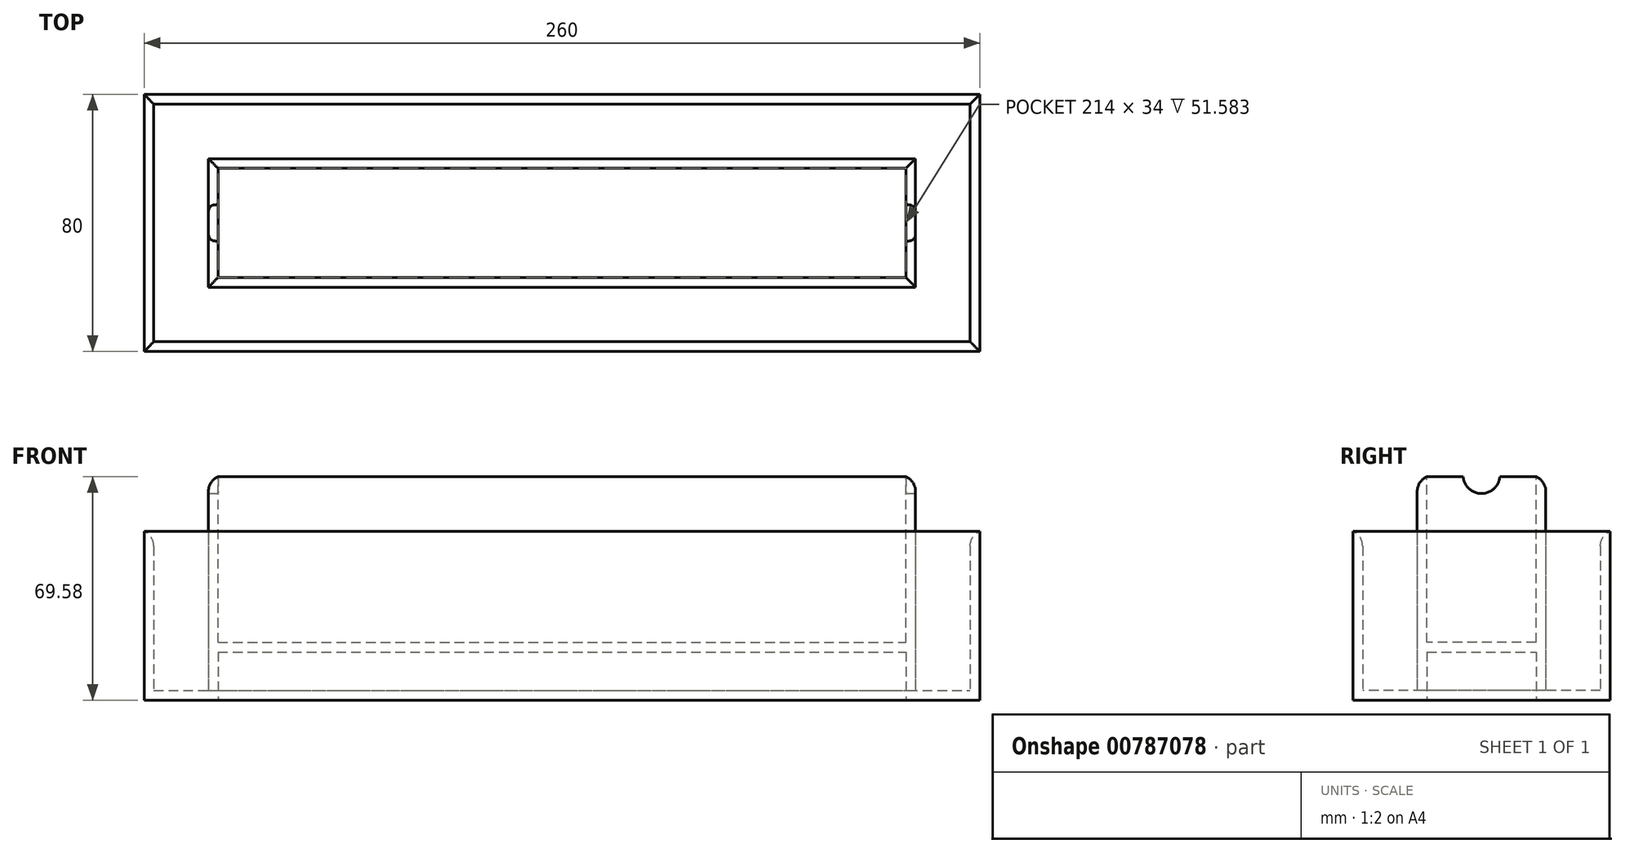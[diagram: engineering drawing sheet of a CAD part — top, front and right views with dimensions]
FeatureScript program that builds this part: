
annotation { "Feature Type Name" : "Feature", "Feature Type Description" : "" }
export const myFeature = defineFeature(function(context is Context, id is Id, definition is map)
    precondition{}
    {
        {
            var Q0;
            Q0=qCreatedBy(makeId("Top.planeOp"),FACE);
            var sketch = newSketch(context, id + "F0", { "sketchPlane" : qUnion([Q0])});
            skLineSegment(sketch, "E0.bottom", {"start": v(-130, 40) * mm, "end": v(130, 40) * mm});
            skLineSegment(sketch, "E0.top", {"start": v(-130, -40) * mm, "end": v(130, -40) * mm});
            skLineSegment(sketch, "E0.left", {"start": v(-130, 40) * mm, "end": v(-130, -40) * mm});
            skLineSegment(sketch, "E0.right", {"start": v(130, 40) * mm, "end": v(130, -40) * mm});
            skSolve(sketch);
        }
        {
            var Q0;
            Q0 = qSketchRegion(id + "F0", true);
            extrude(context, id + "F1", {"entities" : qUnion([Q0]), "depth" : 1 * mm, "offsetDistance" : 25 * mm});
        }
        {
            var Q0;
            Q0=makeQuery(id+"F1.opExtrude","CAP_FACE",FACE,{"disambiguationData":[OSD([sQuery(id+"F0.wireOp",EDGE,"E0.bottom"),sQuery(id+"F0.wireOp",EDGE,"E0.top"),sQuery(id+"F0.wireOp",EDGE,"E0.left"),sQuery(id+"F0.wireOp",EDGE,"E0.right")])],"isStart":false});
            var sketch = newSketch(context, id + "F2", { "sketchPlane" : qUnion([Q0])});
            skLineSegment(sketch, "E1.bottom", {"start": v(-130, 40) * mm, "end": v(-120, 40) * mm});
            skLineSegment(sketch, "E1.top", {"start": v(-130, 30) * mm, "end": v(-120, 30) * mm});
            skLineSegment(sketch, "E1.left", {"start": v(-130, 40) * mm, "end": v(-130, 30) * mm});
            skLineSegment(sketch, "E1.right", {"start": v(-120, 40) * mm, "end": v(-120, 30) * mm});
            skLineSegment(sketch, "E2.bottom", {"start": v(130, 40) * mm, "end": v(120, 40) * mm});
            skLineSegment(sketch, "E2.top", {"start": v(130, 30) * mm, "end": v(120, 30) * mm});
            skLineSegment(sketch, "E2.left", {"start": v(130, 40) * mm, "end": v(130, 30) * mm});
            skLineSegment(sketch, "E2.right", {"start": v(120, 40) * mm, "end": v(120, 30) * mm});
            skLineSegment(sketch, "E3.bottom", {"start": v(-130, -40) * mm, "end": v(-120, -40) * mm});
            skLineSegment(sketch, "E3.top", {"start": v(-130, -30) * mm, "end": v(-120, -30) * mm});
            skLineSegment(sketch, "E3.left", {"start": v(-130, -40) * mm, "end": v(-130, -30) * mm});
            skLineSegment(sketch, "E3.right", {"start": v(-120, -40) * mm, "end": v(-120, -30) * mm});
            skLineSegment(sketch, "E4.bottom", {"start": v(130, -40) * mm, "end": v(120, -40) * mm});
            skLineSegment(sketch, "E4.top", {"start": v(130, -30) * mm, "end": v(120, -30) * mm});
            skLineSegment(sketch, "E4.left", {"start": v(130, -40) * mm, "end": v(130, -30) * mm});
            skLineSegment(sketch, "E4.right", {"start": v(120, -40) * mm, "end": v(120, -30) * mm});
            skSolve(sketch);
        }
        {
            var Q0;
            Q0 = qSketchRegion(id + "F2", true);
            extrude(context, id + "F3", {"entities" : qUnion([Q0]), "operationType" : NewBodyOperationType.ADD, "depth" : 50 * mm, "offsetDistance" : 25 * mm});
        }
        {
            var Q0;
            Q0=makeQuery(id+"F1.opExtrude","CAP_FACE",FACE,{"disambiguationData":[OSD([sQuery(id+"F0.wireOp",EDGE,"E0.bottom"),sQuery(id+"F0.wireOp",EDGE,"E0.top"),sQuery(id+"F0.wireOp",EDGE,"E0.left"),sQuery(id+"F0.wireOp",EDGE,"E0.right")])],"isStart":true});
            shell(context, id + "F4", {"entities" : qUnion([Q0]), "thickness" : 1 * mm});
        }
        {
            var Q0;
            Q0=makeQuery(id+"F3.opExtrude","CAP_FACE",FACE,{"disambiguationData":[OSD([sQuery(id+"F2.wireOp",EDGE,"E3.bottom"),sQuery(id+"F2.wireOp",EDGE,"E3.top"),sQuery(id+"F2.wireOp",EDGE,"E3.left"),sQuery(id+"F2.wireOp",EDGE,"E3.right")])],"isStart":false});
            var sketch = newSketch(context, id + "F5", { "sketchPlane" : qUnion([Q0])});
            skLineSegment(sketch, "E5.bottom", {"start": v(-130, -40) * mm, "end": v(130, -40) * mm});
            skLineSegment(sketch, "E5.top", {"start": v(-130, 40) * mm, "end": v(130, 40) * mm});
            skLineSegment(sketch, "E5.left", {"start": v(-130, -40) * mm, "end": v(-130, 40) * mm});
            skLineSegment(sketch, "E5.right", {"start": v(130, -40) * mm, "end": v(130, 40) * mm});
            skSolve(sketch);
        }
        {
            var Q0;
            Q0 = qSketchRegion(id + "F5", true);
            extrude(context, id + "F6", {"entities" : qUnion([Q0]), "operationType" : NewBodyOperationType.ADD, "depth" : 3 * mm, "offsetDistance" : 25 * mm});
        }
        {
            var Q0;
            Q0=makeQuery(id+"F6.opExtrude","CAP_FACE",FACE,{"disambiguationData":[OSD([sQuery(id+"F5.wireOp",EDGE,"E5.bottom"),sQuery(id+"F5.wireOp",EDGE,"E5.top"),sQuery(id+"F5.wireOp",EDGE,"E5.left"),sQuery(id+"F5.wireOp",EDGE,"E5.right")])],"isStart":false});
            var sketch = newSketch(context, id + "F7", { "sketchPlane" : qUnion([Q0])});
            skLineSegment(sketch, "E6.bottom", {"start": v(-130, 40) * mm, "end": v(130, 40) * mm});
            skLineSegment(sketch, "E6.top", {"start": v(-130, -40) * mm, "end": v(130, -40) * mm});
            skLineSegment(sketch, "E6.left", {"start": v(-130, 40) * mm, "end": v(-130, -40) * mm});
            skLineSegment(sketch, "E6.right", {"start": v(130, 40) * mm, "end": v(130, -40) * mm});
            skLineSegment(sketch, "E7.bottom", {"start": v(-127, 37) * mm, "end": v(127, 37) * mm});
            skLineSegment(sketch, "E7.top", {"start": v(-127, -37) * mm, "end": v(127, -37) * mm});
            skLineSegment(sketch, "E7.left", {"start": v(-127, 37) * mm, "end": v(-127, -37) * mm});
            skLineSegment(sketch, "E7.right", {"start": v(127, 37) * mm, "end": v(127, -37) * mm});
            skSolve(sketch);
        }
        {
            var Q0;
            Q0 = qSketchRegion(id + "F7", true);
            extrude(context, id + "F8", {"entities" : qUnion([Q0]), "operationType" : NewBodyOperationType.ADD, "depth" : 50 * mm, "offsetDistance" : 25 * mm});
        }
        {
            var Q0;
            Q0=makeQuery(id+"F6.opExtrude","CAP_FACE",FACE,{"disambiguationData":[OSD([sQuery(id+"F5.wireOp",EDGE,"E5.bottom"),sQuery(id+"F5.wireOp",EDGE,"E5.top"),sQuery(id+"F5.wireOp",EDGE,"E5.left"),sQuery(id+"F5.wireOp",EDGE,"E5.right")])],"isStart":false});
            var sketch = newSketch(context, id + "F9", { "sketchPlane" : qUnion([Q0])});
            skLineSegment(sketch, "E8.bottom", {"start": v(-110, 20) * mm, "end": v(110, 20) * mm});
            skLineSegment(sketch, "E8.top", {"start": v(-110, -20) * mm, "end": v(110, -20) * mm});
            skLineSegment(sketch, "E8.left", {"start": v(-110, 20) * mm, "end": v(-110, -20) * mm});
            skLineSegment(sketch, "E8.right", {"start": v(110, 20) * mm, "end": v(110, -20) * mm});
            skSolve(sketch);
        }
        {
            var Q0;
            Q0 = qSketchRegion(id + "F9", true);
            extrude(context, id + "F10", {"entities" : qUnion([Q0]), "operationType" : NewBodyOperationType.ADD, "depth" : 67 * mm, "offsetDistance" : 25 * mm});
        }
        {
            var Q0;
            Q0=makeQuery(id+"F10.opExtrude","CAP_FACE",FACE,{"disambiguationData":[OSD([sQuery(id+"F9.wireOp",EDGE,"E8.bottom"),sQuery(id+"F9.wireOp",EDGE,"E8.top"),sQuery(id+"F9.wireOp",EDGE,"E8.left"),sQuery(id+"F9.wireOp",EDGE,"E8.right")])],"isStart":false});
            var sketch = newSketch(context, id + "F11", { "sketchPlane" : qUnion([Q0])});
            skLineSegment(sketch, "E9.bottom", {"start": v(-107, 17) * mm, "end": v(107, 17) * mm});
            skLineSegment(sketch, "E9.top", {"start": v(-107, -17) * mm, "end": v(107, -17) * mm});
            skLineSegment(sketch, "E9.left", {"start": v(-107, 17) * mm, "end": v(-107, -17) * mm});
            skLineSegment(sketch, "E9.right", {"start": v(107, 17) * mm, "end": v(107, -17) * mm});
            skSolve(sketch);
        }
        {
            var Q0;
            Q0 = qSketchRegion(id + "F11", true);
            extrude(context, id + "F12", {"entities" : qUnion([Q0]), "operationType" : NewBodyOperationType.REMOVE, "oppositeDirection" : true, "depth" : 52 * mm, "offsetDistance" : 25 * mm});
        }
        {
            var Q0;
            Q0=makeQuery(id+"F6.opExtrude","CAP_FACE",FACE,{"disambiguationData":[OSD([sQuery(id+"F5.wireOp",EDGE,"E5.bottom"),sQuery(id+"F5.wireOp",EDGE,"E5.top"),sQuery(id+"F5.wireOp",EDGE,"E5.left"),sQuery(id+"F5.wireOp",EDGE,"E5.right")])],"isStart":true});
            var sketch = newSketch(context, id + "F13", { "sketchPlane" : qUnion([Q0])});
            skLineSegment(sketch, "E10.bottom", {"start": v(-107, 17) * mm, "end": v(107, 17) * mm});
            skLineSegment(sketch, "E10.top", {"start": v(-107, -17) * mm, "end": v(107, -17) * mm});
            skLineSegment(sketch, "E10.left", {"start": v(-107, 17) * mm, "end": v(-107, -17) * mm});
            skLineSegment(sketch, "E10.right", {"start": v(107, 17) * mm, "end": v(107, -17) * mm});
            skSolve(sketch);
        }
        {
            var Q0;
            Q0 = qSketchRegion(id + "F13", true);
            extrude(context, id + "F14", {"entities" : qUnion([Q0]), "operationType" : NewBodyOperationType.REMOVE, "oppositeDirection" : true, "depth" : 15 * mm, "offsetDistance" : 25 * mm});
        }
        {
            var Q0;
            Q0=makeQuery(id+"F10.opExtrude","CAP_EDGE",EDGE,{"disambiguationData":[OSD([sQuery(id+"F9.wireOp",EDGE,"E8.top")])],"isStart":false});
            var Q1;
            Q1=makeQuery(id+"F10.opExtrude","CAP_EDGE",EDGE,{"disambiguationData":[OSD([sQuery(id+"F9.wireOp",EDGE,"E8.left")])],"isStart":false});
            var Q2;
            Q2=makeQuery(id+"F10.opExtrude","CAP_EDGE",EDGE,{"disambiguationData":[OSD([sQuery(id+"F9.wireOp",EDGE,"E8.bottom")])],"isStart":false});
            var Q3;
            Q3=makeQuery(id+"F10.opExtrude","CAP_EDGE",EDGE,{"disambiguationData":[OSD([sQuery(id+"F9.wireOp",EDGE,"E8.right")])],"isStart":false});
            var Q4;
            Q4=makeQuery(id+"F8.opExtrude","CAP_EDGE",EDGE,{"disambiguationData":[OSD([sQuery(id+"F7.wireOp",EDGE,"E7.top")])],"isStart":false});
            var Q5;
            Q5=makeQuery(id+"F8.opExtrude","CAP_EDGE",EDGE,{"disambiguationData":[OSD([sQuery(id+"F7.wireOp",EDGE,"E7.right")])],"isStart":false});
            var Q6;
            Q6=makeQuery(id+"F8.opExtrude","CAP_EDGE",EDGE,{"disambiguationData":[OSD([sQuery(id+"F7.wireOp",EDGE,"E7.left")])],"isStart":false});
            var Q7;
            Q7=makeQuery(id+"F8.opExtrude","CAP_EDGE",EDGE,{"disambiguationData":[OSD([sQuery(id+"F7.wireOp",EDGE,"E7.bottom")])],"isStart":false});
            fillet(context, id + "F15", {"entities" : qUnion([Q0, Q1, Q2, Q3, Q4, Q5, Q6, Q7]), "radius" : 5 * mm, "tangentPropagation" : true, "allowEdgeOverflow" : false});
        }
        {
            var Q0;
            Q0=makeQuery(id+"F10.opExtrude","SWEPT_FACE",FACE,{"disambiguationData":[OSD([sQuery(id+"F9.wireOp",EDGE,"E8.right")])]});
            var sketch = newSketch(context, id + "F16", { "sketchPlane" : qUnion([Q0])});
            skPoint(sketch, "E11.centerSnap0", {"position": v(0, 116) * mm});
            skCircle(sketch, "E12", {"center": v(0, 121.07) * mm, "radius": 5.73 * mm});
            skSolve(sketch);
        }
        {
            var Q0;
            Q0 = qSketchRegion(id + "F16", true);
            extrude(context, id + "F17", {"entities" : qUnion([Q0]), "operationType" : NewBodyOperationType.REMOVE, "oppositeDirection" : true, "depth" : 500 * mm, "offsetDistance" : 25 * mm});
        }
        {
            var Q0;
            Q0=makeQuery(id+"F1.opExtrude","CAP_FACE",FACE,{"disambiguationData":[OSD([sQuery(id+"F0.wireOp",EDGE,"E0.bottom"),sQuery(id+"F0.wireOp",EDGE,"E0.top"),sQuery(id+"F0.wireOp",EDGE,"E0.left"),sQuery(id+"F0.wireOp",EDGE,"E0.right")])],"isStart":true});
            var sketch = newSketch(context, id + "F18", { "sketchPlane" : qUnion([Q0])});
            skLineSegment(sketch, "E13.bottom", {"start": v(-130, 40) * mm, "end": v(130, 40) * mm});
            skLineSegment(sketch, "E13.top", {"start": v(-130, -40) * mm, "end": v(130, -40) * mm});
            skLineSegment(sketch, "E13.left", {"start": v(-130, 40) * mm, "end": v(-130, -40) * mm});
            skLineSegment(sketch, "E13.right", {"start": v(130, 40) * mm, "end": v(130, -40) * mm});
            skSolve(sketch);
        }
        {
            var Q0;
            Q0 = qSketchRegion(id + "F18", true);
            extrude(context, id + "F19", {"entities" : qUnion([Q0]), "operationType" : NewBodyOperationType.REMOVE, "oppositeDirection" : true, "depth" : 51 * mm, "offsetDistance" : 25 * mm});
        }
    });
